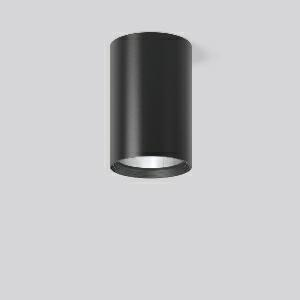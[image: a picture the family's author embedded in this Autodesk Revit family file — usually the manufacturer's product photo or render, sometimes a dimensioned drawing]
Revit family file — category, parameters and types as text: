
# Revit family: heledon_maxi_a_931245_003_2_5f12
name_source: partatom
category: Lighting Fixtures
units: mm (PartAtom-declared; Revit-internal decimal feet)

## family parameters
Cut with Voids When Loaded = No
Host = Face
Light Source = No
Part Type = Normal
Room Calculation Point = No
Round Connector Dimension = Use Diameter
Shared = No

## types (1)
- HELEDON maxi A (1 x LED Modul 927 bakery, 3400 lm, 2700)
    Apparent Load = 33 VA
    Approval mark = CE
    CIE Flux Codes = 100 100 100 100 100
    Color Rendering = 90
    Color Temperature = 2700
    Default Elevation = 1800 mm
    Description = Series: HELEDON maxi
Cylindrical surface-mounted downlight. Housing: die-cast aluminium, powder-coated. Internal ceiling frame polycarbonate with bayonet mounting. Black plastic ring and recessed LED to prevent glare from the side. Optical assembly with reflector made of MIRO-Silver with 98% total light reflection for outstanding efficiency - can be changed without tools. Special LED for illumination of pastries included. Suitable for Ceiling mounting. Easy installation with a separate ceiling frame with bayonet mounting and plug connection. Driver integrated. Connected via plug-in connector. High quality converter without flickering and stroboscopic effect. The following accessories can be mounted without use of tools: interchangeable lenses, decorative glasses, honeycomb louvre, clear and frosted diffusers, white interchangeable plastic ring. 
Colour: deep black, matt (RAL 9005)
Diameter: 123 mm
Height: 183 mm
Lamp: LED
Socket: without socket
Colour temperature: bakery
Colour rendering index (CRI): 97
System power: 33 W
Rated luminous flux: 3400 lm
Luminous efficiency: 103 lm/W
Control gear: Regulated power supply
Protection class: I
Type of protection: IP 20
    Height = 183 mm
    Lamp = 1 x LED Modul 927 bakery
    Lamp Light Flux = 3400 lm
    Lamp count = 1
    Length = 123 mm
    Lifetime = 50000 h
    Luminous efficacy = 103 lm/W
    Manufacturer = RZB
    ModVariant = No
    Model = 931245.003.2
    Mounting Place = Ceiling
    Mounting Type = Surface mounted
    Number of Poles = 1
    OnlyDefault = Yes
    Power Factor = 1
    Product Name = HELEDON maxi A
    Product group = Surface mounted downlights
    ProductGroupID = 302
    Protection Class = Protection class I
    Protection Degree = IP 20
    RLX_Detail_Level = 1
    RLX_Emergency_Light_Flux = 0 lm
    RLX_Emergency_Type = 0
    RLX_Emergency_Type_DB = No
    RlxData = <blob elided: 97325 chars, md5=7214ce77>
    Socket = socket
    Standby Power = 0 W
    System Light Flux = 3400 lm
    System Power = 33 W
    Type Comments = Product without accessories
    Type Image = 931192.003.jpg
    URL = http://relux.com
    VarID = ---
    Voltage = 230 V
    Voltage Range = 220-240 V
    Weight = 0.00 kg
    Width = 0 mm  [stored 0 ft]

note: [stored X ft] marks values corroborated as IEEE doubles in the binary element streams (Revit-internal decimal feet)

## geometry (parser evidence)
native form markers: Blend x4, Sweep x9
no freeform markers — native parametric forms only
